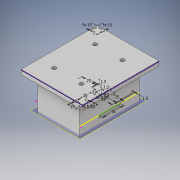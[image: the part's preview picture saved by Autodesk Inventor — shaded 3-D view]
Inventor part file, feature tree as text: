
AUTODESK INVENTOR PART (.ipt)
format: ipt  version: 2019 (Build 230136000, 136)  size: 419,840 bytes
history: native  units: in
note: dims shown in document units (in); Inventor stores cm internally (conversion verified against a paired STEP export)
features: extrude x22, sketch x20, plane x5, fillet x2, other x1, hole x1, chamfer x1
ambient origin geometry x8: Origin, YZ Plane, XZ Plane, XY Plane, X Axis, Y Axis, Z Axis, Center Point
bodies: Solid1 (feature_tree)
feature tree (52):
  plane  "Work Plane1"
  sketch  "Sketch1"  dims[d0=0.9843in d1=0.0067in]
  extrude  "Extrusion1"  Depth=0.9843in
  extrude  "End"  Depth=0.1969in
  extrude  "EndII"  Depth=0.112in
  extrude  "Extrusion4"  Depth=0.112in
  sketch  "Sketch8"  dims[d11=0.1969in d13=0.1969in]
  extrude  "Extrusion8"  Depth=0.1969in
  plane  "Work Plane2"
  sketch  "Sketch12"  dims[d18=2.3278in d19=0.0in d20=0.9843in d21=0.0in]
  other  "Work Point1"
  extrude  "Extrusion10"  Depth=0.9843in TaperAngle=0.0deg
  plane  "Work Plane3"
  extrude  "Extrusion11"  Depth=0.1969in
  plane  "Work Plane4"
  sketch  "Sketch18"  dims[d28=0.0394in d29=0.0394in]
  extrude  "Extrusion15"  Depth=0.0591in TaperAngle=0.0deg
  extrude  "Extrusion16"  Depth=0.0394in
  extrude  "Extrusion17"  [1 undecoded]
  hole  "Hole2"  [1 undecoded]
  sketch  "Sketch19"  dims[d36=0.0039in d37=0.0in d38=-0.1181in]
  extrude  "Extrusion18"  Depth=0.0197in
  extrude  "Extrusion19"  TaperAngle=90.0deg  [1 undecoded]
  extrude  "Extrusion20"  Depth=0.1969in TaperAngle=0.0deg
  extrude  "Extrusion21"  Depth=1.4961in
  extrude  "Extrusion22"  Depth=0.9843in
  extrude  "Extrusion23"  Depth=0.9843in
  fillet  "Fillet1"  Radius=0.9843in
  sketch  "Sketch25"  dims[d51=90.0deg d52=0.0197in]
  extrude  "Extrusion25"  Depth=0.9843in
  sketch  "Sketch28"  dims[d55=1.4961in d56=0.1969in d57=0.0in]
  extrude  "Extrusion27"  Depth=0.3937in
  sketch  "Sketch30"  dims[d60=0.9843in d80=0.9843in]
  extrude  "Extrusion28"  Depth=0.3937in TaperAngle=0.0deg
  extrude  "Extrusion29"  Depth=0.5906in
  chamfer  "Chamfer1"  Distance=0.5906in
  fillet  "Fillet5"  Radius=0.5906in
  extrude  "Extrusion30"  Depth=0.5906in
  plane  "Work Plane6"
  extrude  "Extrusion31"  Depth=0.0787in
  sketch  "Sketch3"  dims[d2=0.1969in d3=0.1969in]
  sketch  "Sketch4"  dims[d4=0.1122in d5=0.112in]
  sketch  "Sketch7"  dims[d7=0.112in d8=0.112in]
  sketch  "Sketch15"  dims[d22=0.9843in d23=0.0in d24=0.1969in]
  sketch  "Sketch17"  dims[d25=0.8661in d26=0.0591in d27=0.0in]
  sketch  "Sketch23"  dims[d49=0.0787in d50=0.0787in]
  sketch  "Sketch26"  dims[d53=0.0in d54=90.0deg]
  sketch  "Sketch29"  dims[d58=0.9843in d59=1.4961in]
  sketch  "Sketch31"  dims[d81=0.9843in d82=0.9843in d83=0.9843in d84=0.9843in d85=0.9843in]
  sketch  "Sketch32"  dims[d86=0.9843in d87=0.9843in d88=0.9843in d89=0.9843in]
  sketch  "Sketch33"  dims[d90=0.9843in d91=0.9843in]
  sketch  "Sketch34"  dims[d96=0.2756in d97=0.75in d98=0.4528in d99=1.5748in d100=0.5635in d101=1.0in d102=0.8108in d103=0.3937in d104=0.3937in d105=0.0in d106=0.5906in d107=0.5906in d108=0.5906in d109=0.5906in d110=0.0787in d111=0.0787in d112=0.0787in d113=0.0787in d120=0.0394in d121=0.0in d122=0.2953in d123=0.0in d124=0.1969in d125=0.0in d126=1.378in d127=0.1181in d128=1.2992in d129=0.6496in d130=0.0in d131=0.1235in d132=0.0in d133=1.1012in d134=0.0in d135=0.0787in d136=0.0787in d137=2.2879in d138=0.0in d139=0.0591in d140=0.0591in d141=0.0591in d142=0.0in d143=0.0394in d144=0.0394in d145=0.0394in d146=0.0394in d147=0.0394in d148=0.0394in d149=0.0394in d150=0.0394in d151=1.1024in d152=0.0in d153=0.0591in d154=0.0591in d155=0.0591in d156=0.0591in d157=0.0591in d158=0.0591in d159=0.0591in d160=0.1181in d161=0.0in d162=0.2362in d163=0.0in d164=0.0567in d168=1.5438in d169=0.0in d171=0.1969in d175=2.3622in d177=0.3937in d178=0.3937in d179=0.5678in d180=1.8937in d181=0.0in d182=0.9188in d183=0.0in d186=0.9188in d187=0.0in d188=1.1024in d189=0.2662in d190=0.0787in d191=45.0deg d192=0.3716in d193=0.0394in d194=0.0354in d195=0.0in d196=-0.1969in d197=0.0in d198=0.0in d199=0.8661in]
note: 3 required parameter values undecoded (feature->parameter linkage not recoverable at this tier; creation-order binding heuristic only, values carry confidence <= 0.55)
